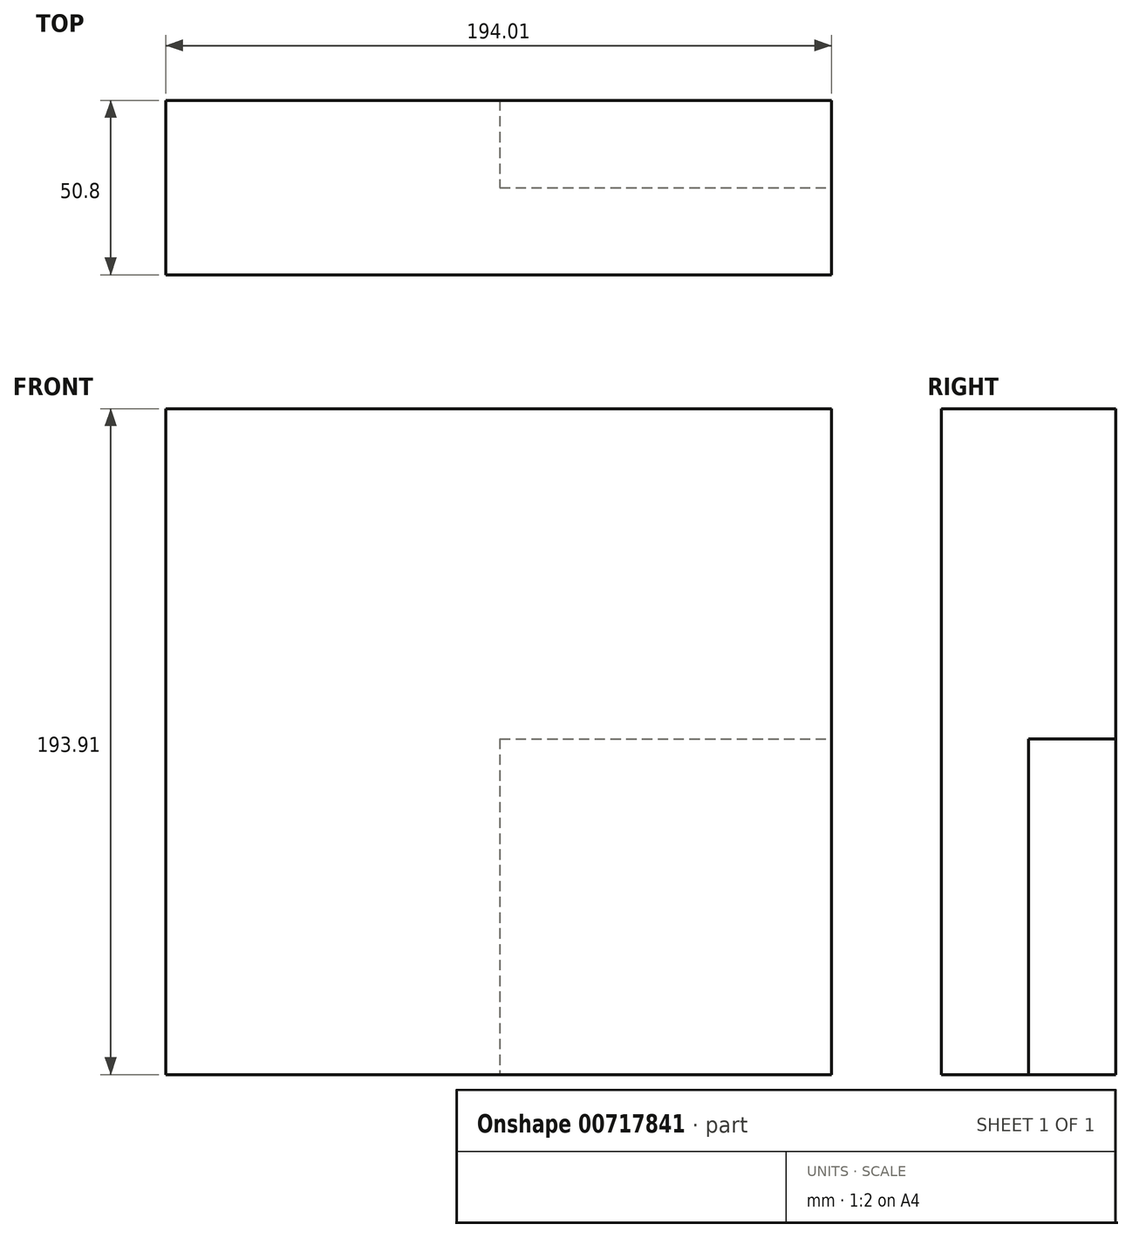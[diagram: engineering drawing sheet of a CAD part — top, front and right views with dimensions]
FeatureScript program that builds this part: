
annotation { "Feature Type Name" : "Feature", "Feature Type Description" : "" }
export const myFeature = defineFeature(function(context is Context, id is Id, definition is map)
    precondition{}
    {
        {
            var Q0;
            Q0=qCreatedBy(makeId("Front.planeOp"),FACE);
            var sketch = newSketch(context, id + "F0", { "sketchPlane" : qUnion([Q0])});
            skLineSegment(sketch, "E0.bottom", {"start": v(-97.38, 96.12) * mm, "end": v(96.63, 96.12) * mm});
            skLineSegment(sketch, "E0.top", {"start": v(-97.38, -97.79) * mm, "end": v(96.63, -97.79) * mm});
            skLineSegment(sketch, "E0.left", {"start": v(-97.38, 96.12) * mm, "end": v(-97.38, -97.79) * mm});
            skLineSegment(sketch, "E0.right", {"start": v(96.63, 96.12) * mm, "end": v(96.63, -97.79) * mm});
            skSolve(sketch);
        }
        {
            var Q0;
            Q0 = qSketchRegion(id + "F0", true);
            extrude(context, id + "F1", {"entities" : qUnion([Q0]), "depth" : 25.4 * mm, "offsetDistance" : 25.4 * mm});
        }
        {
            var Q0;
            Q0=makeQuery(id+"F1.opExtrude","CAP_FACE",FACE,{"disambiguationData":[OSD([sQuery(id+"F0.wireOp",EDGE,"E0.bottom"),sQuery(id+"F0.wireOp",EDGE,"E0.top"),sQuery(id+"F0.wireOp",EDGE,"E0.left"),sQuery(id+"F0.wireOp",EDGE,"E0.right")])],"isStart":true});
            var sketch = newSketch(context, id + "F2", { "sketchPlane" : qUnion([Q0])});
            skLineSegment(sketch, "E1.bottom", {"start": v(0, 0) * mm, "end": v(76.48, 0) * mm});
            skLineSegment(sketch, "E1.top", {"start": v(0, -76.2) * mm, "end": v(76.48, -76.2) * mm});
            skLineSegment(sketch, "E1.left", {"start": v(0, 0) * mm, "end": v(0, -76.2) * mm});
            skLineSegment(sketch, "E1.right", {"start": v(76.48, 0) * mm, "end": v(76.48, -76.2) * mm});
            skLineSegment(sketch, "E2.bottom", {"start": v(76.48, 0) * mm, "end": v(-74.58, 0) * mm});
            skLineSegment(sketch, "E2.top", {"start": v(76.48, 75.6) * mm, "end": v(-74.58, 75.6) * mm});
            skLineSegment(sketch, "E2.left", {"start": v(76.48, 0) * mm, "end": v(76.48, 75.6) * mm});
            skLineSegment(sketch, "E2.right", {"start": v(-74.58, 0) * mm, "end": v(-74.58, 75.6) * mm});
            skPoint(sketch, "E3.firstSnap0", {"position": v(0.95, 75.6) * mm});
            skLineSegment(sketch, "E3.bottom", {"start": v(0, 75.6) * mm, "end": v(0, 75.6) * mm});
            skLineSegment(sketch, "E3.top", {"start": v(0, 0) * mm, "end": v(0, 0) * mm});
            skLineSegment(sketch, "E3.left", {"start": v(0, 75.6) * mm, "end": v(0, 0) * mm});
            skLineSegment(sketch, "E3.right", {"start": v(0, 75.6) * mm, "end": v(0, 0) * mm});
            skLineSegment(sketch, "E4.bottom", {"start": v(0, 0) * mm, "end": v(97.38, 0) * mm});
            skLineSegment(sketch, "E4.top", {"start": v(0, -97.79) * mm, "end": v(97.38, -97.79) * mm});
            skLineSegment(sketch, "E4.left", {"start": v(0, 0) * mm, "end": v(0, -97.79) * mm});
            skLineSegment(sketch, "E4.right", {"start": v(97.38, 0) * mm, "end": v(97.38, -97.79) * mm});
            skLineSegment(sketch, "E5.bottom", {"start": v(97.38, 0) * mm, "end": v(-96.63, 0) * mm});
            skLineSegment(sketch, "E5.top", {"start": v(97.38, 96.12) * mm, "end": v(-96.63, 96.12) * mm});
            skLineSegment(sketch, "E5.left", {"start": v(97.38, 0) * mm, "end": v(97.38, 96.12) * mm});
            skLineSegment(sketch, "E5.right", {"start": v(-96.63, 0) * mm, "end": v(-96.63, 96.12) * mm});
            skSolve(sketch);
        }
        {
            var Q0;
            Q0 = qSketchRegion(id + "F2", true);
            extrude(context, id + "F3", {"entities" : qUnion([Q0]), "operationType" : NewBodyOperationType.ADD, "depth" : 25.4 * mm, "offsetDistance" : 25.4 * mm});
        }
    });
